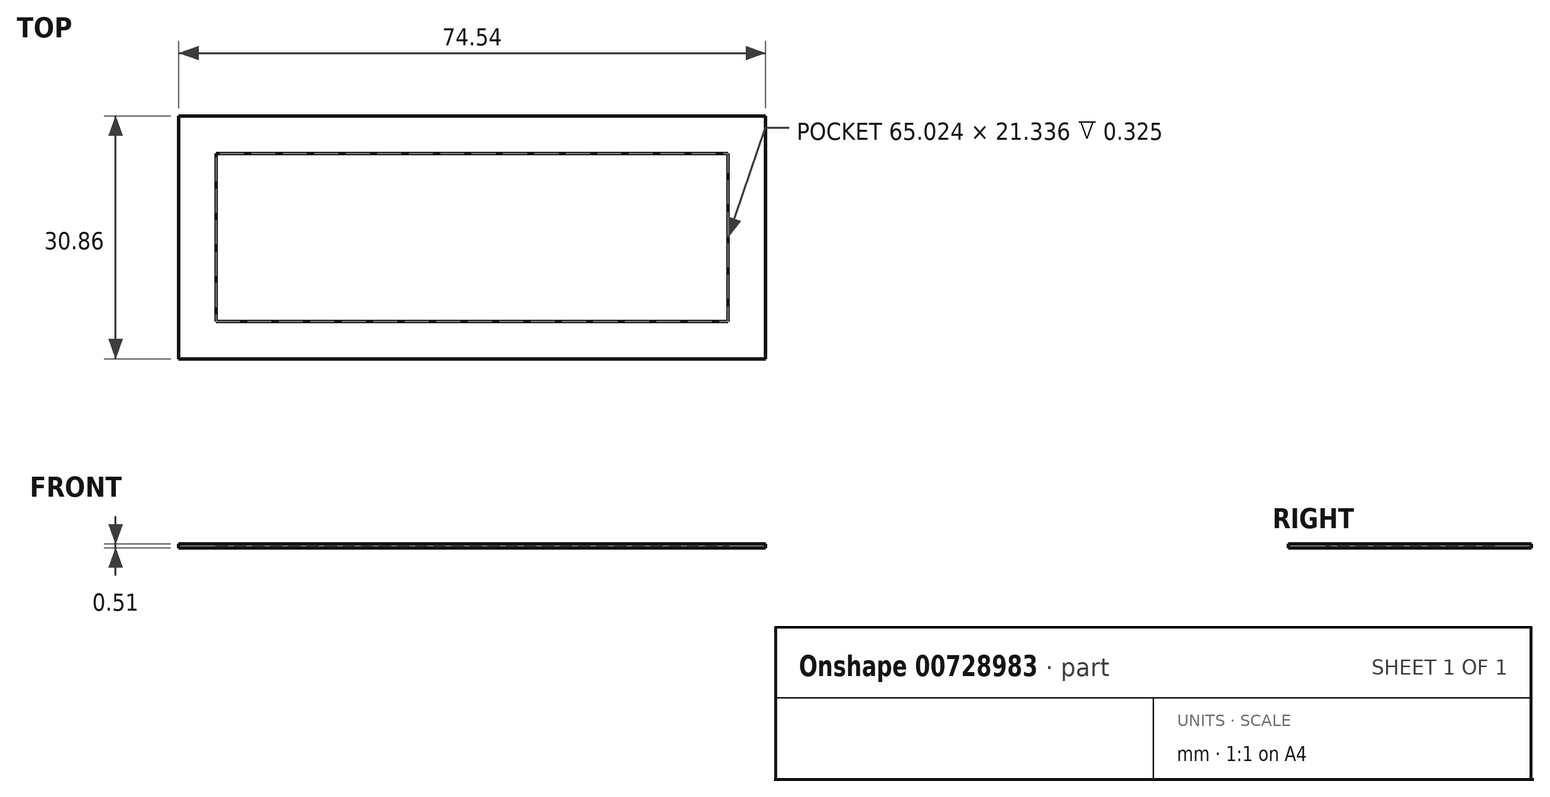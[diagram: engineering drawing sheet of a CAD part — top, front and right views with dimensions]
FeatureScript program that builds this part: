
annotation { "Feature Type Name" : "Feature", "Feature Type Description" : "" }
export const myFeature = defineFeature(function(context is Context, id is Id, definition is map)
    precondition{}
    {
        {
            assignVariable(context, id + "F0", {"name" : "Thick", "anyValue" : 3 / 16});
        }
        {
            var Q0;
            Q0=qCreatedBy(makeId("Top.planeOp"),FACE);
            var sketch = newSketch(context, id + "F1", { "sketchPlane" : qUnion([Q0])});
            skLineSegment(sketch, "E0", {"start": v(-37.27, 15.43) * mm, "end": v(37.27, 15.43) * mm});
            skLineSegment(sketch, "E1", {"start": v(37.27, 15.43) * mm, "end": v(37.27, 10.67) * mm});
            skLineSegment(sketch, "E2", {"start": v(37.27, 10.67) * mm, "end": v(32.51, 10.67) * mm});
            skLineSegment(sketch, "E3", {"start": v(32.51, 10.67) * mm, "end": v(-32.51, 10.67) * mm});
            skLineSegment(sketch, "E4", {"start": v(-32.51, 10.67) * mm, "end": v(-37.27, 10.67) * mm});
            skLineSegment(sketch, "E5", {"start": v(-37.27, 10.67) * mm, "end": v(-37.27, 15.43) * mm});
            skLineSegment(sketch, "E6", {"start": v(-37.27, 10.67) * mm, "end": v(-37.27, -15.43) * mm});
            skLineSegment(sketch, "E7", {"start": v(-37.27, -15.43) * mm, "end": v(-32.51, -15.43) * mm});
            skLineSegment(sketch, "E8", {"start": v(32.51, -15.43) * mm, "end": v(37.27, -15.43) * mm});
            skLineSegment(sketch, "E9", {"start": v(37.27, -15.43) * mm, "end": v(37.27, 10.67) * mm});
            skLineSegment(sketch, "E10", {"start": v(-32.51, -15.43) * mm, "end": v(32.51, -15.43) * mm});
            skLineSegment(sketch, "E11", {"start": v(-32.51, 10.67) * mm, "end": v(-32.51, -10.67) * mm});
            skLineSegment(sketch, "E12", {"start": v(-32.51, -10.67) * mm, "end": v(32.51, -10.67) * mm});
            skLineSegment(sketch, "E13", {"start": v(32.51, -10.67) * mm, "end": v(32.51, 10.67) * mm});
            skLineSegment(sketch, "E14", {"start": v(-32.51, -10.67) * mm, "end": v(-32.51, -15.43) * mm});
            skLineSegment(sketch, "E15", {"start": v(32.51, -10.67) * mm, "end": v(32.51, -15.43) * mm});
            skSolve(sketch);
        }
        {
            var Q0;
            Q0=makeQuery(id+"F1.imprint","IMPRINT",FACE,{"disambiguationData":[TD([[makeQuery(id+"F1.imprint","IMPRINT",EDGE,{"derivedFrom":sQuery(id+"F1.wireOp",EDGE,"E3")}),1.0]])]});
            extrude(context, id + "F2", {"entities" : qUnion([Q0]), "depth" : (getVariable(context, 'Thick')) * mm, "offsetDistance" : 25.4 * mm});
        }
        {
            var Q0;
            Q0=makeQuery(id+"F1.imprint","IMPRINT",FACE,{"disambiguationData":[TD([[makeQuery(id+"F1.imprint","IMPRINT",EDGE,{"derivedFrom":sQuery(id+"F1.wireOp",EDGE,"E0")}),-1.0]])]});
            var Q1;
            Q1=makeQuery(id+"F1.imprint","IMPRINT",FACE,{"disambiguationData":[TD([[makeQuery(id+"F1.imprint","IMPRINT",EDGE,{"derivedFrom":sQuery(id+"F1.wireOp",EDGE,"E2")}),1.0]])]});
            var Q2;
            Q2=makeQuery(id+"F1.imprint","IMPRINT",FACE,{"disambiguationData":[TD([[makeQuery(id+"F1.imprint","IMPRINT",EDGE,{"derivedFrom":sQuery(id+"F1.wireOp",EDGE,"E10")}),1.0]])]});
            var Q3;
            Q3=makeQuery(id+"F1.imprint","IMPRINT",FACE,{"disambiguationData":[TD([[makeQuery(id+"F1.imprint","IMPRINT",EDGE,{"derivedFrom":sQuery(id+"F1.wireOp",EDGE,"E4")}),1.0]])]});
            extrude(context, id + "F3", {"entities" : qUnion([Q0, Q1, Q2, Q3]), "operationType" : NewBodyOperationType.ADD, "depth" : (.325 + getVariable(context, 'Thick')) * mm, "offsetDistance" : 25.4 * mm});
        }
    });
